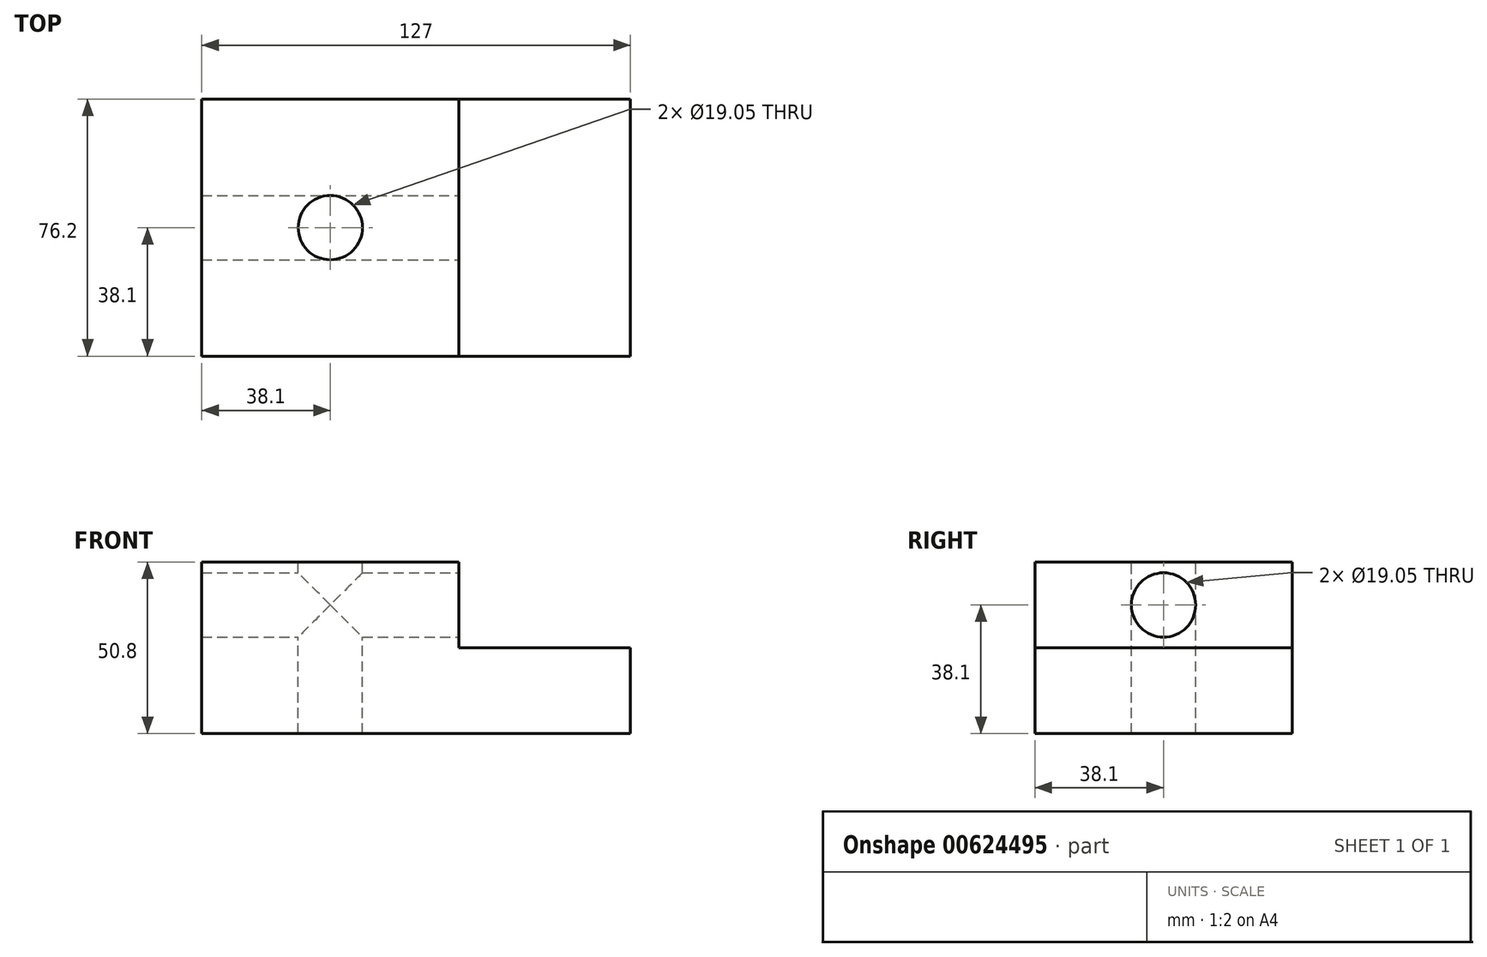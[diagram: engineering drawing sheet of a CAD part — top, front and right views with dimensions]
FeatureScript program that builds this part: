
annotation { "Feature Type Name" : "Feature", "Feature Type Description" : "" }
export const myFeature = defineFeature(function(context is Context, id is Id, definition is map)
    precondition{}
    {
        {
            var Q0;
            Q0=qCreatedBy(makeId("Front.planeOp"),FACE);
            var sketch = newSketch(context, id + "F0", { "sketchPlane" : qUnion([Q0])});
            skLineSegment(sketch, "E0.bottom", {"start": v(0, 0) * mm, "end": v(127, 0) * mm});
            skLineSegment(sketch, "E0.top", {"start": v(0, 50.8) * mm, "end": v(76.2, 50.8) * mm});
            skLineSegment(sketch, "E0.left", {"start": v(0, 0) * mm, "end": v(0, 50.8) * mm});
            skLineSegment(sketch, "E0.right", {"start": v(127, 0) * mm, "end": v(127, 25.4) * mm});
            skLineSegment(sketch, "E1.top", {"start": v(127, 25.4) * mm, "end": v(76.2, 25.4) * mm});
            skLineSegment(sketch, "E1.right", {"start": v(76.2, 50.8) * mm, "end": v(76.2, 25.4) * mm});
            skSolve(sketch);
        }
        {
            var Q0;
            Q0 = qSketchRegion(id + "F0", true);
            extrude(context, id + "F1", {"entities" : qUnion([Q0]), "depth" : 76.2 * mm, "offsetDistance" : 25.4 * mm});
        }
        {
            var Q0;
            Q0=makeQuery(id+"F1.opExtrude","SWEPT_FACE",FACE,{"disambiguationData":[OSD([sQuery(id+"F0.wireOp",EDGE,"E0.top")])]});
            var sketch = newSketch(context, id + "F2", { "sketchPlane" : qUnion([Q0])});
            skLineSegment(sketch, "E2", {"start": v(0, -76.2) * mm, "end": v(76.2, 0) * mm});
            skLineSegment(sketch, "E3", {"start": v(76.2, -76.2) * mm, "end": v(0, 0) * mm});
            skPoint(sketch, "E4.center.orphan", {"position": v(38.1, -38.1) * mm});
            skSolve(sketch);
        }
        {
            var Q0;
            Q0=sQuery(id+"F2.wireOp",VERTEX,"E4.center.orphan");
            var Q1;
            Q1=makeQuery(id+"F1.opExtrude","SWEPT_BODY",BODY,{"disambiguationData":[OSD([sQuery(id+"F0.wireOp",EDGE,"E0.bottom"),sQuery(id+"F0.wireOp",EDGE,"E0.top"),sQuery(id+"F0.wireOp",EDGE,"E0.left"),sQuery(id+"F0.wireOp",EDGE,"E0.right"),sQuery(id+"F0.wireOp",EDGE,"E1.top"),sQuery(id+"F0.wireOp",EDGE,"E1.right")])]});
            hole(context, id + "F3", {"style" : HoleStyle.SIMPLE, "endStyle" : HoleEndStyle.THROUGH, "holeDiameter" : 19.05 * mm, "majorDiameter" : 6.35 * mm, "isTappedThrough" : true, "tappedDepth" : 12.7 * mm, "tapClearance" : 3, "locations" : qUnion([Q0]), "scope" : qUnion([Q1])});
        }
        {
            var Q0;
            Q0=makeQuery(id+"F1.opExtrude","SWEPT_FACE",FACE,{"disambiguationData":[OSD([sQuery(id+"F0.wireOp",EDGE,"E1.right")])]});
            var sketch = newSketch(context, id + "F4", { "sketchPlane" : qUnion([Q0])});
            skLineSegment(sketch, "E5", {"start": v(-76.2, 50.8) * mm, "end": v(0, 25.4) * mm});
            skLineSegment(sketch, "E6", {"start": v(0, 50.8) * mm, "end": v(-76.2, 25.4) * mm});
            skPoint(sketch, "E7", {"position": v(-38.1, 38.1) * mm});
            skSolve(sketch);
        }
        {
            var Q0;
            Q0=sQuery(id+"F4.wireOp",VERTEX,"E7");
            var Q1;
            Q1=makeQuery(id+"F1.opExtrude","SWEPT_BODY",BODY,{"disambiguationData":[OSD([sQuery(id+"F0.wireOp",EDGE,"E0.bottom"),sQuery(id+"F0.wireOp",EDGE,"E0.top"),sQuery(id+"F0.wireOp",EDGE,"E0.left"),sQuery(id+"F0.wireOp",EDGE,"E0.right"),sQuery(id+"F0.wireOp",EDGE,"E1.top"),sQuery(id+"F0.wireOp",EDGE,"E1.right")])]});
            hole(context, id + "F5", {"style" : HoleStyle.SIMPLE, "endStyle" : HoleEndStyle.THROUGH, "holeDiameter" : 19.05 * mm, "majorDiameter" : 6.35 * mm, "isTappedThrough" : true, "tappedDepth" : 12.7 * mm, "tapClearance" : 3, "locations" : qUnion([Q0]), "scope" : qUnion([Q1])});
        }
    });
